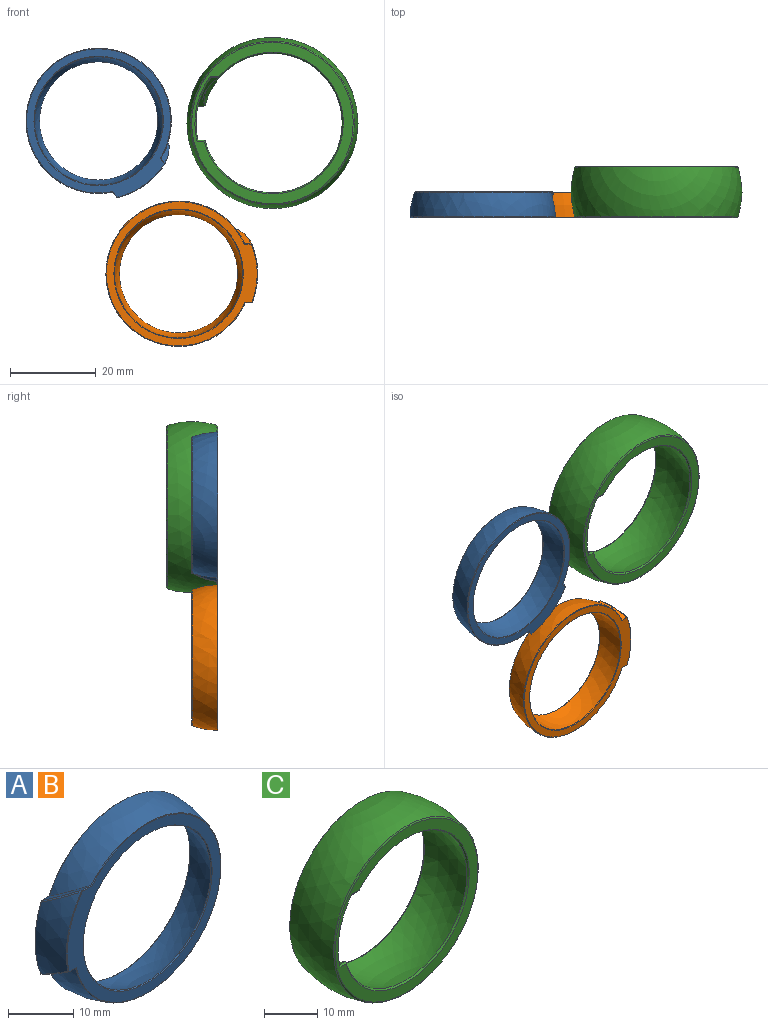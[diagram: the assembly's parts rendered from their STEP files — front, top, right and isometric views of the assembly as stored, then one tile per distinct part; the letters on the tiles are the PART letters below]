
ASSEMBLY  parts=3 mates=2
PART A: 19 faces, bbox 35.5x34x34 mm
  f0: sphere r=15mm, area 536.1mm2, adj f11,f16
  f1: plane 33.22x31.63mm, normal (0,-1,0), area 197.6mm2, adj f12,f13,f14,f15,f16,f17
  f2: sphere r=17mm, area 532.3mm2, adj f3,f5,f8,f10,f14,f15
  f3: plane 5.74x4.7mm, normal (0,0.5,0.87), area 10.3mm2, adj f2,f9,f10,f14,f18
  f4: sphere r=18.5mm, area 81.5mm2, adj f7,f12,f17,f18
  f5: plane 5.74x3.31mm, normal (0,-0.5,-0.87), area 9.3mm2, adj f2,f8,f13,f15,f17
  f6: plane 35.24x33.74mm, normal (0,1,0), area 195.6mm2, adj f7,f8,f9,f10,f11
  f7: cone r=18.37mm half-angle=44.8deg, axis (0,-1,0), area 2.6mm2, adj f4,f6,f8,f9,f17,f18
  f8: plane 1.68x0.2mm, normal (0,0.5,-0.87), area 0.4mm2, adj f2,f5,f6,f7,f10,f17
  f9: plane 1.63x0.11mm, normal (0,0.87,0.5), area 0.2mm2, adj f3,f6,f7,f10,f18
  f10: cone r=17mm half-angle=44.8deg, axis (0,-1,0), area 17.2mm2, adj f2,f3,f6,f8,f9
  f11: cone r=15.13mm half-angle=45.2deg, axis (0,1,0), area 17.5mm2, adj f0,f6
  f12: cone r=17.53mm half-angle=54.3deg, axis (0,1,0), area 2.2mm2, adj f1,f4,f14,f17,f18
  f13: plane 1.59x0.11mm, normal (0,-0.87,-0.5), area 0.2mm2, adj f1,f5,f15,f17
  f14: plane 2.07x0.2mm, normal (0,-0.5,0.87), area 0.4mm2, adj f1,f2,f3,f12,f15,f18
  f15: cone r=15.82mm half-angle=55.2deg, axis (0,1,0), area 12.7mm2, adj f1,f2,f5,f13,f14
  f16: cone r=13.83mm half-angle=33.6deg, axis (0,-1,0), area 19mm2, adj f0,f1
  f17: cone r=17.3mm half-angle=54.1deg, axis (0,0.5,0.87), area 2.2mm2, adj f1,f4,f5,f7,f8,f12,f13
  f18: cone r=17.56mm half-angle=54.1deg, axis (0,-0.5,-0.87), area 2.4mm2, adj f3,f4,f7,f9,f12,f14
PART B: same geometry as A
PART C: 19 faces, bbox 40x40x40 mm
  f0: plane 11.46x6.61mm, normal (0,-0.5,-0.87), area 19.7mm2, adj f1,f9,f12,f14,f15,f17
  f1: sphere r=18.75mm, area 171.3mm2, adj f0,f2,f7,f9,f12,f13
  f2: plane 11.46x6.61mm, normal (0,0.5,0.87), area 19.7mm2, adj f1,f7,f8,f10,f13,f18
  f3: sphere r=17.25mm, area 1043.8mm2, adj f10,f15,f17,f18
  f4: plane 37.76x37.76mm, normal (0,1,0), area 232.8mm2, adj f7,f8,f9,f10,f11
  f5: plane 37.76x37.76mm, normal (0,-1,0), area 232.8mm2, adj f12,f13,f14,f15,f16
  f6: sphere r=20mm, area 1459.1mm2, adj f11,f16
  f7: cone r=17.88mm half-angle=36.2deg, axis (0,1,0), area 6.8mm2, adj f1,f2,f4,f8,f9
  f8: plane 2.08x0.24mm, normal (0,0.87,0.5), area 0.5mm2, adj f2,f4,f7,f10
  f9: plane 1.8x0.41mm, normal (0,0.5,-0.87), area 0.8mm2, adj f0,f1,f4,f7,f10,f17
  f10: cone r=16.56mm half-angle=35.5deg, axis (0,1,0), area 38.8mm2, adj f2,f3,f4,f8,f9,f17,f18
  f11: cone r=19.14mm half-angle=53.4deg, axis (0,-1,0), area 38.8mm2, adj f4,f6
  f12: cone r=18.14mm half-angle=36.2deg, axis (0,-1,0), area 6.8mm2, adj f0,f1,f5,f13,f14
  f13: plane 1.8x0.41mm, normal (0,-0.5,0.87), area 0.8mm2, adj f1,f2,f5,f12,f15,f18
  f14: plane 2.08x0.24mm, normal (0,-0.87,-0.5), area 0.5mm2, adj f0,f5,f12,f15
  f15: cone r=16.3mm half-angle=35.5deg, axis (0,-1,0), area 38.8mm2, adj f0,f3,f5,f13,f14,f17,f18
  f16: cone r=18.88mm half-angle=53.4deg, axis (0,1,0), area 38.8mm2, adj f5,f6
  f17: cone r=16.01mm half-angle=55.9deg, axis (0,-0.5,-0.87), area 4.6mm2, adj f0,f3,f9,f10,f15
  f18: cone r=16.28mm half-angle=55.9deg, axis (0,0.5,0.87), area 4.6mm2, adj f2,f3,f10,f13,f15
PLACE A rot(axis=(-0.46,0,-0.89),180deg) t=(-36.37,-0.98,4.34)mm
PLACE B rot(axis=(0,0,1),180deg) t=(-17.68,-0.98,-31.39)mm
PLACE C t=(4.26,5.02,3.84)mm fixed
MATE planar B.f6 <-> C.f5  axis (0,-1,0) through (-2.27,-0.98,-24.54)mm
MATE planar A.f6 <-> B.f6  axis (0,-1,0) through (-35.32,-0.98,2.84)mm
